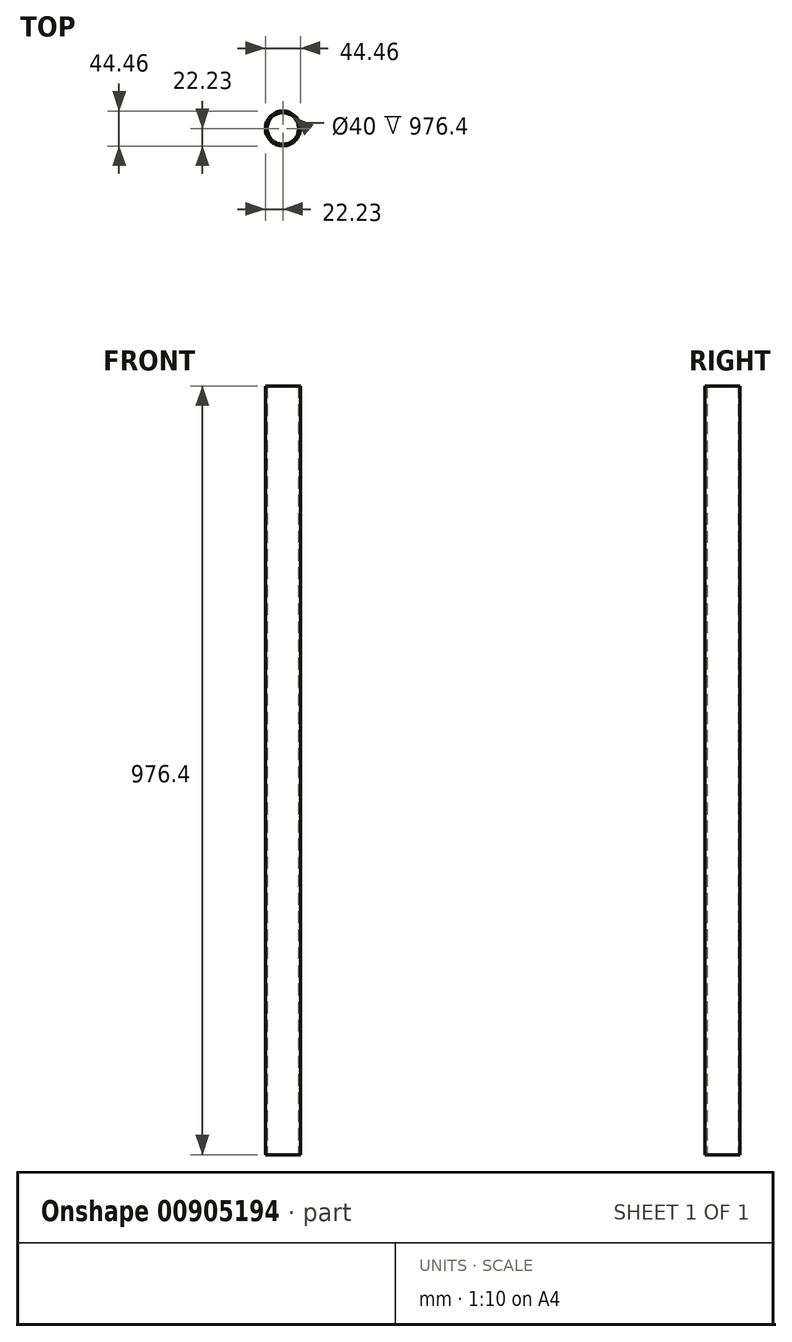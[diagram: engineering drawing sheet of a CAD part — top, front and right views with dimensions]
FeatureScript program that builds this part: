
annotation { "Feature Type Name" : "Feature", "Feature Type Description" : "" }
export const myFeature = defineFeature(function(context is Context, id is Id, definition is map)
    precondition{}
    {
        {
            var Q0;
            Q0=qCreatedBy(makeId("Top.planeOp"),FACE);
            var sketch = newSketch(context, id + "F0", { "sketchPlane" : qUnion([Q0])});
            skCircle(sketch, "E0", {"center": v(0, 0) * mm, "radius": 22.23 * mm});
            skCircle(sketch, "E1", {"center": v(0, 0) * mm, "radius": 20 * mm});
            skSolve(sketch);
        }
        {
            var Q0;
            Q0 = qSketchRegion(id + "F0", true);
            extrude(context, id + "F1", {"entities" : qUnion([Q0]), "depth" : 976.4 * mm, "offsetDistance" : 25 * mm});
        }
    });
